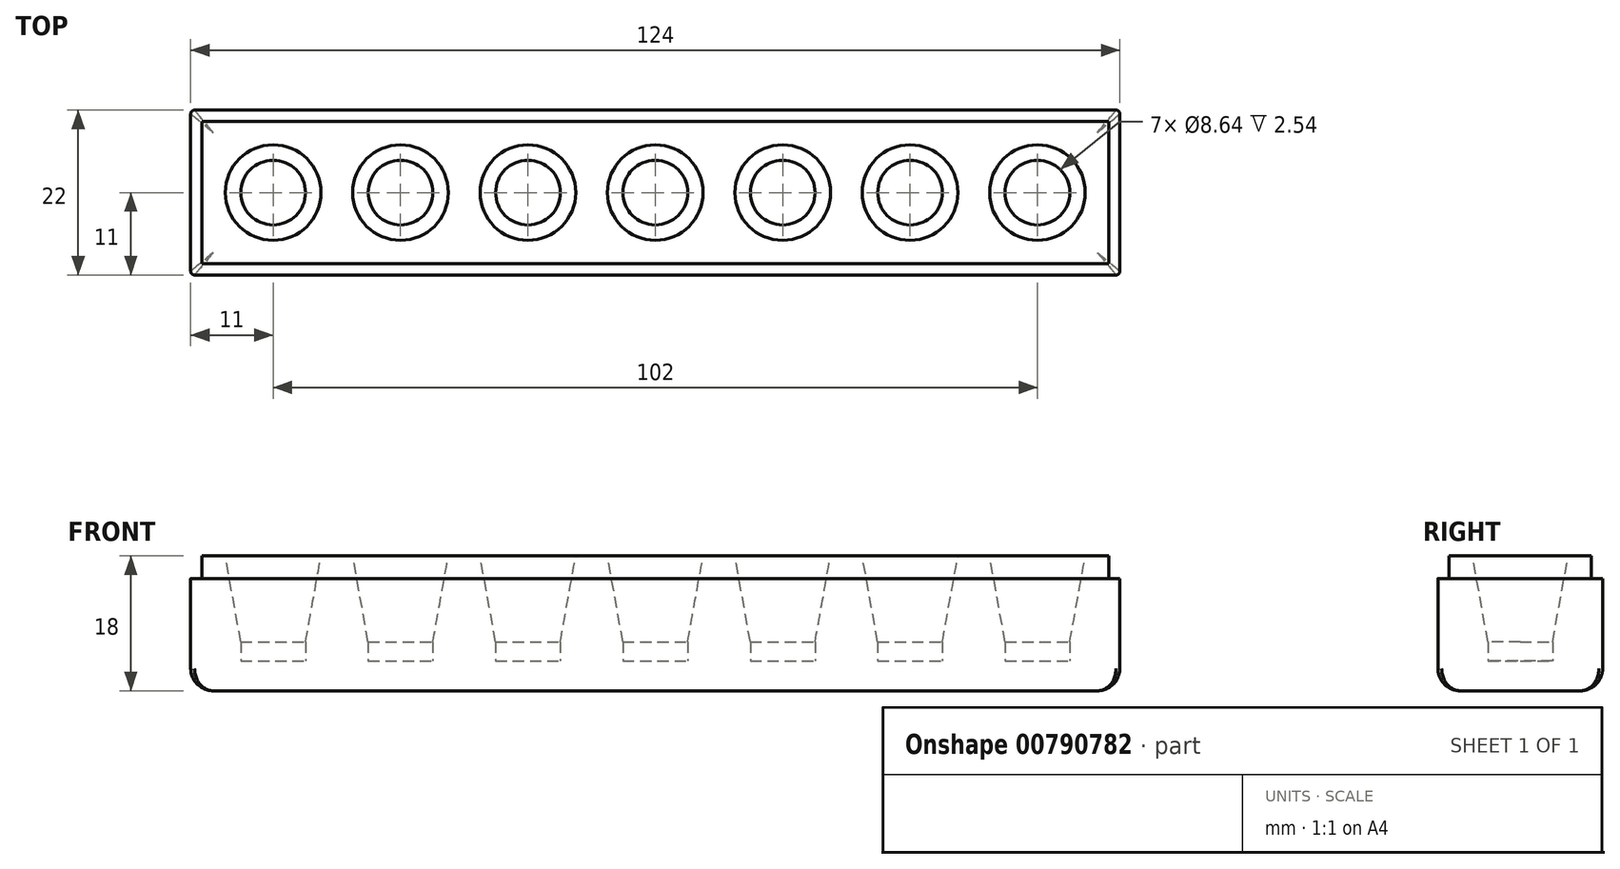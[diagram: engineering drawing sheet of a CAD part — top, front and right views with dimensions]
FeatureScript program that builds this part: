
annotation { "Feature Type Name" : "Feature", "Feature Type Description" : "" }
export const myFeature = defineFeature(function(context is Context, id is Id, definition is map)
    precondition{}
    {
        {
            var Q0;
            Q0=qCreatedBy(makeId("Front.planeOp"),FACE);
            var sketch = newSketch(context, id + "F0", { "sketchPlane" : qUnion([Q0])});
            skLineSegment(sketch, "E0", {"start": v(0, 0) * mm, "end": v(0, 20.32) * mm, "construction": true});
            skLineSegment(sketch, "E1", {"start": v(-5.33, 20.32) * mm, "end": v(-5.33, 17.78) * mm});
            skLineSegment(sketch, "E2", {"start": v(-5.33, 17.78) * mm, "end": v(-6.6, 17.78) * mm});
            skLineSegment(sketch, "E3", {"start": v(-6.6, 17.78) * mm, "end": v(-6.6, 15.24) * mm});
            skLineSegment(sketch, "E4", {"start": v(-4.32, 0) * mm, "end": v(-4.32, 2.54) * mm});
            skLineSegment(sketch, "E5", {"start": v(-4.32, 2.54) * mm, "end": v(-6.6, 15.24) * mm});
            skLineSegment(sketch, "E6", {"start": v(-2.03, 0) * mm, "end": v(-2.54, 0) * mm});
            skLineSegment(sketch, "E7", {"start": v(-5.33, 20.32) * mm, "end": v(0, 20.32) * mm});
            skLineSegment(sketch, "E8", {"start": v(-4.32, 0) * mm, "end": v(0, 0) * mm});
            skLineSegment(sketch, "E9", {"start": v(0, 0) * mm, "end": v(0, 20.32) * mm});
            skSolve(sketch);
        }
        {
            var Q0;
            Q0=qCreatedBy(makeId("Top.planeOp"),FACE);
            var sketch = newSketch(context, id + "F1", { "sketchPlane" : qUnion([Q0])});
            skLineSegment(sketch, "E10.bottom", {"start": v(-62, -11) * mm, "end": v(62, -11) * mm});
            skLineSegment(sketch, "E10.top", {"start": v(-62, 11) * mm, "end": v(62, 11) * mm});
            skLineSegment(sketch, "E10.left", {"start": v(-62, -11) * mm, "end": v(-62, 11) * mm});
            skLineSegment(sketch, "E10.right", {"start": v(62, -11) * mm, "end": v(62, 11) * mm});
            skPoint(sketch, "E10.middle", {"position": v(0, 0) * mm});
            skSolve(sketch);
        }
        {
            var Q0;
            Q0=makeQuery(id+"F0.imprint","IMPRINT",FACE,{"disambiguationData":[TD([[makeQuery(id+"F0.imprint","IMPRINT",EDGE,{"derivedFrom":sQuery(id+"F0.wireOp",EDGE,"E1")}),1.0]])]});
            var Q1;
            Q1=sQuery(id+"F0.wireOp",EDGE,"E9");
            revolve(context, id + "F2", {"surfaceOperationType" : NewSurfaceOperationType.NEW, "entities" : qUnion([Q0]), "axis" : qUnion([Q1]), "revolveType" : RevolveType.FULL});
        }
        {
            var Q0;
            Q0=makeQuery(id+"F2.opRevolve","SWEPT_BODY",BODY,{"disambiguationData":[OSD([sQuery(id+"F0.wireOp",EDGE,"E1"),sQuery(id+"F0.wireOp",EDGE,"E2"),sQuery(id+"F0.wireOp",EDGE,"E3"),sQuery(id+"F0.wireOp",EDGE,"E4"),sQuery(id+"F0.wireOp",EDGE,"E5"),sQuery(id+"F0.wireOp",EDGE,"E7"),sQuery(id+"F0.wireOp",EDGE,"E8"),sQuery(id+"F0.wireOp",EDGE,"E9")])]});
            transform(context, id + "F3", {"entities" : qUnion([Q0]), "transformType" : TransformType.TRANSLATION_3D, "dx" : 17 * mm, "dy" : 0 * mm, "dz" : 0 * mm, "makeCopy" : true});
        }
        {
            var Q0;
            Q0=makeQuery(id+"F2.opRevolve","SWEPT_BODY",BODY,{"disambiguationData":[OSD([sQuery(id+"F0.wireOp",EDGE,"E1"),sQuery(id+"F0.wireOp",EDGE,"E2"),sQuery(id+"F0.wireOp",EDGE,"E3"),sQuery(id+"F0.wireOp",EDGE,"E4"),sQuery(id+"F0.wireOp",EDGE,"E5"),sQuery(id+"F0.wireOp",EDGE,"E7"),sQuery(id+"F0.wireOp",EDGE,"E8"),sQuery(id+"F0.wireOp",EDGE,"E9")])]});
            transform(context, id + "F4", {"entities" : qUnion([Q0]), "transformType" : TransformType.TRANSLATION_3D, "dx" : -17 * mm, "dy" : 0 * mm, "dz" : 0 * mm, "makeCopy" : true});
        }
        {
            var Q0;
            Q0=makeQuery(id+"F4.opPattern","COPY",BODY,{"derivedFrom":makeQuery(id+"F2.opRevolve","SWEPT_BODY",BODY,{"disambiguationData":[OSD([sQuery(id+"F0.wireOp",EDGE,"E1"),sQuery(id+"F0.wireOp",EDGE,"E2"),sQuery(id+"F0.wireOp",EDGE,"E3"),sQuery(id+"F0.wireOp",EDGE,"E4"),sQuery(id+"F0.wireOp",EDGE,"E5"),sQuery(id+"F0.wireOp",EDGE,"E7"),sQuery(id+"F0.wireOp",EDGE,"E8"),sQuery(id+"F0.wireOp",EDGE,"E9")])]}),"instanceName":"1"});
            transform(context, id + "F5", {"entities" : qUnion([Q0]), "transformType" : TransformType.TRANSLATION_3D, "dx" : -17 * mm, "dy" : 0 * mm, "dz" : 0 * mm, "makeCopy" : true});
        }
        {
            var Q0;
            Q0=makeQuery(id+"F5.opPattern","COPY",BODY,{"derivedFrom":makeQuery(id+"F4.opPattern","COPY",BODY,{"derivedFrom":makeQuery(id+"F2.opRevolve","SWEPT_BODY",BODY,{"disambiguationData":[OSD([sQuery(id+"F0.wireOp",EDGE,"E1"),sQuery(id+"F0.wireOp",EDGE,"E2"),sQuery(id+"F0.wireOp",EDGE,"E3"),sQuery(id+"F0.wireOp",EDGE,"E4"),sQuery(id+"F0.wireOp",EDGE,"E5"),sQuery(id+"F0.wireOp",EDGE,"E7"),sQuery(id+"F0.wireOp",EDGE,"E8"),sQuery(id+"F0.wireOp",EDGE,"E9")])]}),"instanceName":"1"}),"instanceName":"1"});
            transform(context, id + "F6", {"entities" : qUnion([Q0]), "transformType" : TransformType.TRANSLATION_3D, "dx" : -17 * mm, "dy" : 0 * mm, "dz" : 0 * mm, "makeCopy" : true});
        }
        {
            var Q0;
            Q0=makeQuery(id+"F3.opPattern","COPY",BODY,{"derivedFrom":makeQuery(id+"F2.opRevolve","SWEPT_BODY",BODY,{"disambiguationData":[OSD([sQuery(id+"F0.wireOp",EDGE,"E1"),sQuery(id+"F0.wireOp",EDGE,"E2"),sQuery(id+"F0.wireOp",EDGE,"E3"),sQuery(id+"F0.wireOp",EDGE,"E4"),sQuery(id+"F0.wireOp",EDGE,"E5"),sQuery(id+"F0.wireOp",EDGE,"E7"),sQuery(id+"F0.wireOp",EDGE,"E8"),sQuery(id+"F0.wireOp",EDGE,"E9")])]}),"instanceName":"1"});
            transform(context, id + "F7", {"entities" : qUnion([Q0]), "transformType" : TransformType.TRANSLATION_3D, "dx" : 17 * mm, "dy" : 0 * mm, "dz" : 0 * mm, "makeCopy" : true});
        }
        {
            var Q0;
            Q0=makeQuery(id+"F7.opPattern","COPY",BODY,{"derivedFrom":makeQuery(id+"F3.opPattern","COPY",BODY,{"derivedFrom":makeQuery(id+"F2.opRevolve","SWEPT_BODY",BODY,{"disambiguationData":[OSD([sQuery(id+"F0.wireOp",EDGE,"E1"),sQuery(id+"F0.wireOp",EDGE,"E2"),sQuery(id+"F0.wireOp",EDGE,"E3"),sQuery(id+"F0.wireOp",EDGE,"E4"),sQuery(id+"F0.wireOp",EDGE,"E5"),sQuery(id+"F0.wireOp",EDGE,"E7"),sQuery(id+"F0.wireOp",EDGE,"E8"),sQuery(id+"F0.wireOp",EDGE,"E9")])]}),"instanceName":"1"}),"instanceName":"1"});
            transform(context, id + "F8", {"entities" : qUnion([Q0]), "transformType" : TransformType.TRANSLATION_3D, "dx" : 17 * mm, "dy" : 0 * mm, "dz" : 0 * mm, "makeCopy" : true});
        }
        {
            var Q0;
            Q0=makeQuery(id+"F2.opRevolve","SWEPT_BODY",BODY,{"disambiguationData":[OSD([sQuery(id+"F0.wireOp",EDGE,"E1"),sQuery(id+"F0.wireOp",EDGE,"E2"),sQuery(id+"F0.wireOp",EDGE,"E3"),sQuery(id+"F0.wireOp",EDGE,"E4"),sQuery(id+"F0.wireOp",EDGE,"E5"),sQuery(id+"F0.wireOp",EDGE,"E7"),sQuery(id+"F0.wireOp",EDGE,"E8"),sQuery(id+"F0.wireOp",EDGE,"E9")])]});
            var Q1;
            Q1=makeQuery(id+"F3.opPattern","COPY",BODY,{"derivedFrom":makeQuery(id+"F2.opRevolve","SWEPT_BODY",BODY,{"disambiguationData":[OSD([sQuery(id+"F0.wireOp",EDGE,"E1"),sQuery(id+"F0.wireOp",EDGE,"E2"),sQuery(id+"F0.wireOp",EDGE,"E3"),sQuery(id+"F0.wireOp",EDGE,"E4"),sQuery(id+"F0.wireOp",EDGE,"E5"),sQuery(id+"F0.wireOp",EDGE,"E7"),sQuery(id+"F0.wireOp",EDGE,"E8"),sQuery(id+"F0.wireOp",EDGE,"E9")])]}),"instanceName":"1"});
            var Q2;
            Q2=makeQuery(id+"F8.opPattern","COPY",BODY,{"derivedFrom":makeQuery(id+"F7.opPattern","COPY",BODY,{"derivedFrom":makeQuery(id+"F3.opPattern","COPY",BODY,{"derivedFrom":makeQuery(id+"F2.opRevolve","SWEPT_BODY",BODY,{"disambiguationData":[OSD([sQuery(id+"F0.wireOp",EDGE,"E1"),sQuery(id+"F0.wireOp",EDGE,"E2"),sQuery(id+"F0.wireOp",EDGE,"E3"),sQuery(id+"F0.wireOp",EDGE,"E4"),sQuery(id+"F0.wireOp",EDGE,"E5"),sQuery(id+"F0.wireOp",EDGE,"E7"),sQuery(id+"F0.wireOp",EDGE,"E8"),sQuery(id+"F0.wireOp",EDGE,"E9")])]}),"instanceName":"1"}),"instanceName":"1"}),"instanceName":"1"});
            var Q3;
            Q3=makeQuery(id+"F5.opPattern","COPY",BODY,{"derivedFrom":makeQuery(id+"F4.opPattern","COPY",BODY,{"derivedFrom":makeQuery(id+"F2.opRevolve","SWEPT_BODY",BODY,{"disambiguationData":[OSD([sQuery(id+"F0.wireOp",EDGE,"E1"),sQuery(id+"F0.wireOp",EDGE,"E2"),sQuery(id+"F0.wireOp",EDGE,"E3"),sQuery(id+"F0.wireOp",EDGE,"E4"),sQuery(id+"F0.wireOp",EDGE,"E5"),sQuery(id+"F0.wireOp",EDGE,"E7"),sQuery(id+"F0.wireOp",EDGE,"E8"),sQuery(id+"F0.wireOp",EDGE,"E9")])]}),"instanceName":"1"}),"instanceName":"1"});
            var Q4;
            Q4=makeQuery(id+"F6.opPattern","COPY",BODY,{"derivedFrom":makeQuery(id+"F5.opPattern","COPY",BODY,{"derivedFrom":makeQuery(id+"F4.opPattern","COPY",BODY,{"derivedFrom":makeQuery(id+"F2.opRevolve","SWEPT_BODY",BODY,{"disambiguationData":[OSD([sQuery(id+"F0.wireOp",EDGE,"E1"),sQuery(id+"F0.wireOp",EDGE,"E2"),sQuery(id+"F0.wireOp",EDGE,"E3"),sQuery(id+"F0.wireOp",EDGE,"E4"),sQuery(id+"F0.wireOp",EDGE,"E5"),sQuery(id+"F0.wireOp",EDGE,"E7"),sQuery(id+"F0.wireOp",EDGE,"E8"),sQuery(id+"F0.wireOp",EDGE,"E9")])]}),"instanceName":"1"}),"instanceName":"1"}),"instanceName":"1"});
            var Q5;
            Q5=makeQuery(id+"F4.opPattern","COPY",BODY,{"derivedFrom":makeQuery(id+"F2.opRevolve","SWEPT_BODY",BODY,{"disambiguationData":[OSD([sQuery(id+"F0.wireOp",EDGE,"E1"),sQuery(id+"F0.wireOp",EDGE,"E2"),sQuery(id+"F0.wireOp",EDGE,"E3"),sQuery(id+"F0.wireOp",EDGE,"E4"),sQuery(id+"F0.wireOp",EDGE,"E5"),sQuery(id+"F0.wireOp",EDGE,"E7"),sQuery(id+"F0.wireOp",EDGE,"E8"),sQuery(id+"F0.wireOp",EDGE,"E9")])]}),"instanceName":"1"});
            var Q6;
            Q6=makeQuery(id+"F7.opPattern","COPY",BODY,{"derivedFrom":makeQuery(id+"F3.opPattern","COPY",BODY,{"derivedFrom":makeQuery(id+"F2.opRevolve","SWEPT_BODY",BODY,{"disambiguationData":[OSD([sQuery(id+"F0.wireOp",EDGE,"E1"),sQuery(id+"F0.wireOp",EDGE,"E2"),sQuery(id+"F0.wireOp",EDGE,"E3"),sQuery(id+"F0.wireOp",EDGE,"E4"),sQuery(id+"F0.wireOp",EDGE,"E5"),sQuery(id+"F0.wireOp",EDGE,"E7"),sQuery(id+"F0.wireOp",EDGE,"E8"),sQuery(id+"F0.wireOp",EDGE,"E9")])]}),"instanceName":"1"}),"instanceName":"1"});
            transform(context, id + "F9", {"entities" : qUnion([Q0, Q1, Q2, Q3, Q4, Q5, Q6]), "transformType" : TransformType.TRANSLATION_3D, "dx" : 0 * mm, "dy" : 0 * mm, "dz" : 4 * mm, "makeCopy" : false});
        }
        {
            var Q0;
            Q0=makeQuery(id+"F1.imprint","IMPRINT",FACE,{"disambiguationData":[TD([[makeQuery(id+"F1.imprint","IMPRINT",EDGE,{"derivedFrom":sQuery(id+"F1.wireOp",EDGE,"E10.bottom")}),1.0]])]});
            extrude(context, id + "F10", {"entities" : qUnion([Q0]), "depth" : 18 * mm, "offsetDistance" : 25 * mm});
        }
        {
            var Q0;
            Q0=makeQuery(id+"F6.opPattern","COPY",BODY,{"derivedFrom":makeQuery(id+"F5.opPattern","COPY",BODY,{"derivedFrom":makeQuery(id+"F4.opPattern","COPY",BODY,{"derivedFrom":makeQuery(id+"F2.opRevolve","SWEPT_BODY",BODY,{"disambiguationData":[OSD([sQuery(id+"F0.wireOp",EDGE,"E1"),sQuery(id+"F0.wireOp",EDGE,"E2"),sQuery(id+"F0.wireOp",EDGE,"E3"),sQuery(id+"F0.wireOp",EDGE,"E4"),sQuery(id+"F0.wireOp",EDGE,"E5"),sQuery(id+"F0.wireOp",EDGE,"E7"),sQuery(id+"F0.wireOp",EDGE,"E8"),sQuery(id+"F0.wireOp",EDGE,"E9")])]}),"instanceName":"1"}),"instanceName":"1"}),"instanceName":"1"});
            var Q1;
            Q1=makeQuery(id+"F5.opPattern","COPY",BODY,{"derivedFrom":makeQuery(id+"F4.opPattern","COPY",BODY,{"derivedFrom":makeQuery(id+"F2.opRevolve","SWEPT_BODY",BODY,{"disambiguationData":[OSD([sQuery(id+"F0.wireOp",EDGE,"E1"),sQuery(id+"F0.wireOp",EDGE,"E2"),sQuery(id+"F0.wireOp",EDGE,"E3"),sQuery(id+"F0.wireOp",EDGE,"E4"),sQuery(id+"F0.wireOp",EDGE,"E5"),sQuery(id+"F0.wireOp",EDGE,"E7"),sQuery(id+"F0.wireOp",EDGE,"E8"),sQuery(id+"F0.wireOp",EDGE,"E9")])]}),"instanceName":"1"}),"instanceName":"1"});
            var Q2;
            Q2=makeQuery(id+"F4.opPattern","COPY",BODY,{"derivedFrom":makeQuery(id+"F2.opRevolve","SWEPT_BODY",BODY,{"disambiguationData":[OSD([sQuery(id+"F0.wireOp",EDGE,"E1"),sQuery(id+"F0.wireOp",EDGE,"E2"),sQuery(id+"F0.wireOp",EDGE,"E3"),sQuery(id+"F0.wireOp",EDGE,"E4"),sQuery(id+"F0.wireOp",EDGE,"E5"),sQuery(id+"F0.wireOp",EDGE,"E7"),sQuery(id+"F0.wireOp",EDGE,"E8"),sQuery(id+"F0.wireOp",EDGE,"E9")])]}),"instanceName":"1"});
            var Q3;
            Q3=makeQuery(id+"F2.opRevolve","SWEPT_BODY",BODY,{"disambiguationData":[OSD([sQuery(id+"F0.wireOp",EDGE,"E1"),sQuery(id+"F0.wireOp",EDGE,"E2"),sQuery(id+"F0.wireOp",EDGE,"E3"),sQuery(id+"F0.wireOp",EDGE,"E4"),sQuery(id+"F0.wireOp",EDGE,"E5"),sQuery(id+"F0.wireOp",EDGE,"E7"),sQuery(id+"F0.wireOp",EDGE,"E8"),sQuery(id+"F0.wireOp",EDGE,"E9")])]});
            var Q4;
            Q4=makeQuery(id+"F3.opPattern","COPY",BODY,{"derivedFrom":makeQuery(id+"F2.opRevolve","SWEPT_BODY",BODY,{"disambiguationData":[OSD([sQuery(id+"F0.wireOp",EDGE,"E1"),sQuery(id+"F0.wireOp",EDGE,"E2"),sQuery(id+"F0.wireOp",EDGE,"E3"),sQuery(id+"F0.wireOp",EDGE,"E4"),sQuery(id+"F0.wireOp",EDGE,"E5"),sQuery(id+"F0.wireOp",EDGE,"E7"),sQuery(id+"F0.wireOp",EDGE,"E8"),sQuery(id+"F0.wireOp",EDGE,"E9")])]}),"instanceName":"1"});
            var Q5;
            Q5=makeQuery(id+"F7.opPattern","COPY",BODY,{"derivedFrom":makeQuery(id+"F3.opPattern","COPY",BODY,{"derivedFrom":makeQuery(id+"F2.opRevolve","SWEPT_BODY",BODY,{"disambiguationData":[OSD([sQuery(id+"F0.wireOp",EDGE,"E1"),sQuery(id+"F0.wireOp",EDGE,"E2"),sQuery(id+"F0.wireOp",EDGE,"E3"),sQuery(id+"F0.wireOp",EDGE,"E4"),sQuery(id+"F0.wireOp",EDGE,"E5"),sQuery(id+"F0.wireOp",EDGE,"E7"),sQuery(id+"F0.wireOp",EDGE,"E8"),sQuery(id+"F0.wireOp",EDGE,"E9")])]}),"instanceName":"1"}),"instanceName":"1"});
            var Q6;
            Q6=makeQuery(id+"F8.opPattern","COPY",BODY,{"derivedFrom":makeQuery(id+"F7.opPattern","COPY",BODY,{"derivedFrom":makeQuery(id+"F3.opPattern","COPY",BODY,{"derivedFrom":makeQuery(id+"F2.opRevolve","SWEPT_BODY",BODY,{"disambiguationData":[OSD([sQuery(id+"F0.wireOp",EDGE,"E1"),sQuery(id+"F0.wireOp",EDGE,"E2"),sQuery(id+"F0.wireOp",EDGE,"E3"),sQuery(id+"F0.wireOp",EDGE,"E4"),sQuery(id+"F0.wireOp",EDGE,"E5"),sQuery(id+"F0.wireOp",EDGE,"E7"),sQuery(id+"F0.wireOp",EDGE,"E8"),sQuery(id+"F0.wireOp",EDGE,"E9")])]}),"instanceName":"1"}),"instanceName":"1"}),"instanceName":"1"});
            var Q7;
            Q7=makeQuery(id+"F10.opExtrude","SWEPT_BODY",BODY,{"disambiguationData":[OSD([sQuery(id+"F1.wireOp",EDGE,"E10.bottom"),sQuery(id+"F1.wireOp",EDGE,"E10.top"),sQuery(id+"F1.wireOp",EDGE,"E10.left"),sQuery(id+"F1.wireOp",EDGE,"E10.right")])]});
            booleanBodies(context, id + "F11", {"operationType" : BooleanOperationType.SUBTRACTION, "tools" : qUnion([Q0, Q1, Q2, Q3, Q4, Q5, Q6]), "targets" : qUnion([Q7])});
        }
        {
            var Q0;
            Q0=makeQuery(id+"F10.opExtrude","CAP_FACE",FACE,{"disambiguationData":[OSD([sQuery(id+"F1.wireOp",EDGE,"E10.bottom"),sQuery(id+"F1.wireOp",EDGE,"E10.top"),sQuery(id+"F1.wireOp",EDGE,"E10.left"),sQuery(id+"F1.wireOp",EDGE,"E10.right")])],"isStart":false});
            var sketch = newSketch(context, id + "F12", { "sketchPlane" : qUnion([Q0])});
            skLineSegment(sketch, "E11.bottom", {"start": v(-60.5, 9.5) * mm, "end": v(60.5, 9.5) * mm});
            skLineSegment(sketch, "E11.top", {"start": v(-60.5, -9.5) * mm, "end": v(60.5, -9.5) * mm});
            skLineSegment(sketch, "E11.left", {"start": v(-60.5, 9.5) * mm, "end": v(-60.5, -9.5) * mm});
            skLineSegment(sketch, "E11.right", {"start": v(60.5, 9.5) * mm, "end": v(60.5, -9.5) * mm});
            skPoint(sketch, "E11.middle", {"position": v(0, 0) * mm});
            skSolve(sketch);
        }
        {
            var Q0;
            Q0=makeQuery(id+"F12.imprint","IMPRINT",FACE,{"disambiguationData":[TD([[makeQuery(id+"F12.imprint","IMPRINT",EDGE,{"derivedFrom":sQuery(id+"F12.wireOp",EDGE,"E11.bottom")}),1.0]])]});
            extrude(context, id + "F13", {"entities" : qUnion([Q0]), "operationType" : NewBodyOperationType.REMOVE, "oppositeDirection" : true, "depth" : 3 * mm, "offsetDistance" : 25 * mm});
        }
        {
            var Q0;
            Q0=makeQuery(id+"F13.boolean.opBoolean","COPY",EDGE,{"derivedFrom":makeQuery(id+"F13.opExtrude","CAP_EDGE",EDGE,{"disambiguationData":[OSD([sQuery(id+"F12.wireOp",EDGE,"E11.top")])],"isStart":true})});
            var Q1;
            Q1=makeQuery(id+"F13.boolean.opBoolean","COPY",EDGE,{"derivedFrom":makeQuery(id+"F13.opExtrude","CAP_EDGE",EDGE,{"disambiguationData":[OSD([sQuery(id+"F12.wireOp",EDGE,"E11.left")])],"isStart":true})});
            var Q2;
            Q2=makeQuery(id+"F13.boolean.opBoolean","COPY",EDGE,{"derivedFrom":makeQuery(id+"F13.opExtrude","CAP_EDGE",EDGE,{"disambiguationData":[OSD([sQuery(id+"F12.wireOp",EDGE,"E11.bottom")])],"isStart":true})});
            var Q3;
            Q3=makeQuery(id+"F13.boolean.opBoolean","COPY",EDGE,{"derivedFrom":makeQuery(id+"F13.opExtrude","CAP_EDGE",EDGE,{"disambiguationData":[OSD([sQuery(id+"F12.wireOp",EDGE,"E11.right")])],"isStart":true})});
            var Q4;
            Q4=makeQuery(id+"F10.opExtrude","SWEPT_EDGE",EDGE,{"disambiguationData":[OSD([sQuery(id+"F1.wireOp",EDGE,"E10.bottom"),sQuery(id+"F1.wireOp",EDGE,"E10.left")])]});
            var Q5;
            Q5=makeQuery(id+"F10.opExtrude","SWEPT_EDGE",EDGE,{"disambiguationData":[OSD([sQuery(id+"F1.wireOp",EDGE,"E10.bottom"),sQuery(id+"F1.wireOp",EDGE,"E10.right")])]});
            var Q6;
            Q6=makeQuery(id+"F10.opExtrude","SWEPT_EDGE",EDGE,{"disambiguationData":[OSD([sQuery(id+"F1.wireOp",EDGE,"E10.top"),sQuery(id+"F1.wireOp",EDGE,"E10.left")])]});
            var Q7;
            Q7=makeQuery(id+"F10.opExtrude","SWEPT_EDGE",EDGE,{"disambiguationData":[OSD([sQuery(id+"F1.wireOp",EDGE,"E10.top"),sQuery(id+"F1.wireOp",EDGE,"E10.right")])]});
            fillet(context, id + "F14", {"entities" : qUnion([Q0, Q1, Q2, Q3, Q4, Q5, Q6, Q7]), "radius" : .5 * mm, "tangentPropagation" : true, "allowEdgeOverflow" : false});
        }
        {
            var Q0;
            Q0=makeQuery(id+"F10.opExtrude","CAP_EDGE",EDGE,{"disambiguationData":[OSD([sQuery(id+"F1.wireOp",EDGE,"E10.top")])],"isStart":true});
            var Q1;
            Q1=makeQuery(id+"F10.opExtrude","CAP_EDGE",EDGE,{"disambiguationData":[OSD([sQuery(id+"F1.wireOp",EDGE,"E10.left")])],"isStart":true});
            fillet(context, id + "F15", {"entities" : qUnion([Q0, Q1]), "radius" : 3 * mm, "tangentPropagation" : true, "allowEdgeOverflow" : false});
        }
    });
